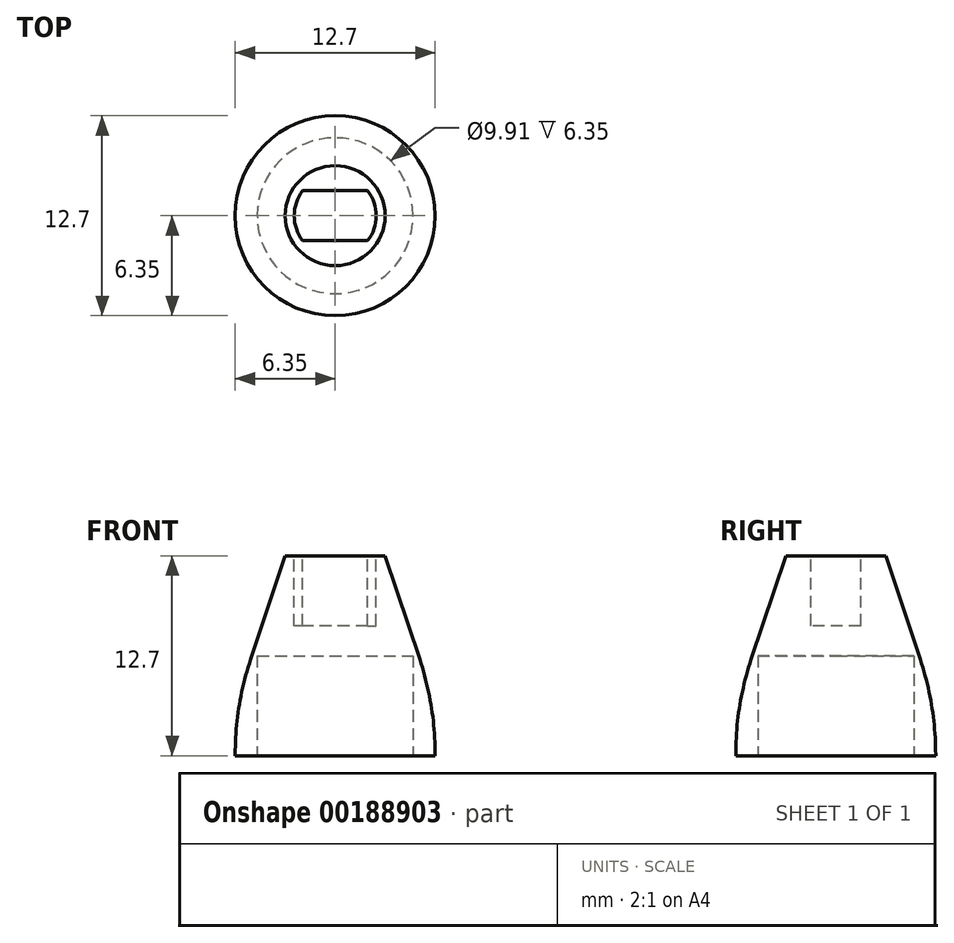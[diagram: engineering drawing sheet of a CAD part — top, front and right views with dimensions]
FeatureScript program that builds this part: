
annotation { "Feature Type Name" : "Feature", "Feature Type Description" : "" }
export const myFeature = defineFeature(function(context is Context, id is Id, definition is map)
    precondition{}
    {
        {
            var Q0;
            Q0=qCreatedBy(makeId("Front.planeOp"),FACE);
            var sketch = newSketch(context, id + "F0", { "sketchPlane" : qUnion([Q0])});
            skLineSegment(sketch, "E0", {"start": v(0, 0) * mm, "end": v(0, 6.35) * mm});
            skLineSegment(sketch, "E1", {"start": v(0, 6.35) * mm, "end": v(-3.18, 6.35) * mm});
            skLineSegment(sketch, "E2", {"start": v(0, 0) * mm, "end": v(0, -6.35) * mm});
            skLineSegment(sketch, "E3", {"start": v(0, -6.35) * mm, "end": v(-6.35, -6.35) * mm});
            skLineSegment(sketch, "E4", {"start": v(-6.35, -6.35) * mm, "end": v(-6.35, -3.18) * mm});
            skLineSegment(sketch, "E5", {"start": v(-3.17, 6.35) * mm, "end": v(-6.35, -3.18) * mm});
            skSolve(sketch);
        }
        {
            var Q0;
            Q0=qSketchRegion(id+"F0",true);
            var Q1;
            Q1=sQuery(id+"F0.wireOp",EDGE,"E0");
            revolve(context, id + "F1", {"entities" : qUnion([Q0]), "axis" : qUnion([Q1]), "revolveType" : RevolveType.FULL});
        }
        {
            var Q0;
            Q0=makeQuery(id+"F1.opRevolve","SWEPT_EDGE",EDGE,{"disambiguationData":[OSD([sQuery(id+"F0.wireOp",EDGE,"E4"),sQuery(id+"F0.wireOp",EDGE,"E5")])]});
            fillet(context, id + "F2", {"entities" : qUnion([Q0]), "radius" : 19.05 * mm, "tangentPropagation" : true, "allowEdgeOverflow" : false});
        }
        {
            var Q0;
            Q0=makeQuery(id+"F1.opRevolve","SWEPT_FACE",FACE,{"disambiguationData":[OSD([sQuery(id+"F0.wireOp",EDGE,"E1")])]});
            var sketch = newSketch(context, id + "F3", { "sketchPlane" : qUnion([Q0])});
            skLineSegment(sketch, "E6.bottom", {"start": v(2.06, 1.59) * mm, "end": v(-2.06, 1.59) * mm});
            skLineSegment(sketch, "E6.top", {"start": v(2.06, -1.59) * mm, "end": v(-2.06, -1.59) * mm});
            skPoint(sketch, "E6.middle", {"position": v(0, 0) * mm});
            skArc(sketch, "E7", {"start": v(-2.06, 1.59) * mm, "mid": v(-2.6, 0) * mm, "end": v(-2.06, -1.59) * mm});
            skPoint(sketch, "E8.orphan", {"position": v(-2.6, 1.59) * mm});
            skArc(sketch, "E9.trimOffspring", {"start": v(2.06, -1.59) * mm, "mid": v(2.6, 0) * mm, "end": v(2.06, 1.59) * mm});
            skPoint(sketch, "E10.orphan", {"position": v(-2.6, -1.59) * mm});
            skPoint(sketch, "E11.orphan", {"position": v(2.6, 1.59) * mm});
            skPoint(sketch, "E12.orphan", {"position": v(2.6, -1.59) * mm});
            skSolve(sketch);
        }
        {
            var Q0;
            Q0=qSketchRegion(id+"F3",true);
            extrude(context, id + "F4", {"entities" : qUnion([Q0]), "operationType" : NewBodyOperationType.REMOVE, "oppositeDirection" : true, "depth" : 4.44 * mm});
        }
        {
            var Q0;
            Q0=makeQuery(id+"F1.opRevolve","SWEPT_FACE",FACE,{"disambiguationData":[OSD([sQuery(id+"F0.wireOp",EDGE,"E3")])]});
            var sketch = newSketch(context, id + "F5", { "sketchPlane" : qUnion([Q0])});
            skCircle(sketch, "E13", {"center": v(0, 0) * mm, "radius": 4.95 * mm});
            skSolve(sketch);
        }
        {
            var Q0;
            Q0=qSketchRegion(id+"F5",true);
            extrude(context, id + "F6", {"entities" : qUnion([Q0]), "operationType" : NewBodyOperationType.REMOVE, "oppositeDirection" : true, "depth" : 6.35 * mm});
        }
    });
